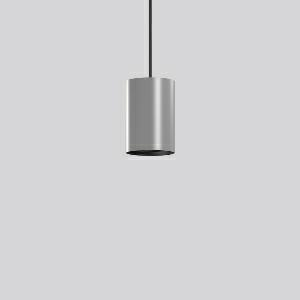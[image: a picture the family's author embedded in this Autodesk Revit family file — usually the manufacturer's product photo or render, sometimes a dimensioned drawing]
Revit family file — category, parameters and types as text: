
# Revit family: deecos_p_maxi_911537_004_2_90a2
name_source: partatom
category: Lighting Fixtures
units: mm (PartAtom-declared; Revit-internal decimal feet)

## family parameters
Cut with Voids When Loaded = No
Host = Face
Light Source = No
Part Type = Normal
Room Calculation Point = No
Round Connector Dimension = Use Diameter
Shared = No

## types (1)
- DEECOS P maxi (1 x LED Modul 927, 4100 lm, 2700)
    Apparent Load = 35 VA
    Approval mark = CE
    CIE Flux Codes = 100 100 100 100 100
    Color Rendering = 92
    Color Temperature = 2700
    Default Elevation = 1800 mm
    Description = Series: DEECOS P maxi
Cylindrical pendant luminaire. Housing: die-cast aluminium, powder-coated. Canopy made of powder-coated sheet steel with magnetic attachment. Optical assembly with reflector made of MIRO-Silver with 98% total light reflection for outstanding efficiency - can be changed without tools. Best colour rendering index Ra>90. Transparent suspension cable 2 m, can be shortened. High quality converter without flickering and stroboscopic effect. The following accessories can be mounted without use of tools: interchangeable lenses, honeycomb louvre, clear and frosted diffusers, white interchangeable plastic ring. Decorative recessed suspension set available as accessory. 
Colour: silver
Diameter: 123 mm
Height: 181 mm
Suspension length: 2000 mm
Lamp: LED
Socket: without socket
Colour temperature: 2700K
Colour rendering index (CRI): 92
System power: 35 W
Rated luminous flux: 4100 lm
Luminous efficiency: 117 lm/W
Control gear: Regulated power supply
Protection class: I
Type of protection: IP 20
    Height = 181 mm
    Lamp = 1 x LED Modul 927
    Lamp Light Flux = 4100 lm
    Lamp count = 1
    Length = 123 mm
    Lifetime = 50000 h
    Luminous efficacy = 117 lm/W
    Manufacturer = RZB
    ModVariant = No
    Model = 911537.004.2
    Mounting Place = Ceiling
    Mounting Type = Pendant
    Number of Poles = 1
    OnlyDefault = Yes
    Power Factor = 1
    Product Name = DEECOS P maxi
    Product group = Pendant luminaires
    ProductGroupID = 902
    Protection Class = Protection class I
    Protection Degree = IP 20
    RLX_Detail_Level = 1
    RLX_Emergency_Light_Flux = 0 lm
    RLX_Emergency_Type = 0
    RLX_Emergency_Type_DB = No
    RlxData = <blob elided: 35749 chars, md5=2c0f9470>
    Socket = socket
    Standby Power = 0 W
    System Light Flux = 4100 lm
    System Power = 35 W
    Type Comments = Product without accessories
    Type Image = 911480.004.jpg
    URL = http://relux.com
    VarID = ---
    Voltage = 230 V
    Voltage Range = 220-240 V
    Weight = 0.00 kg
    Width = 0 mm  [stored 0 ft]

note: [stored X ft] marks values corroborated as IEEE doubles in the binary element streams (Revit-internal decimal feet)

## geometry (parser evidence)
native form markers: Blend x4, Sweep x9
no freeform markers — native parametric forms only
